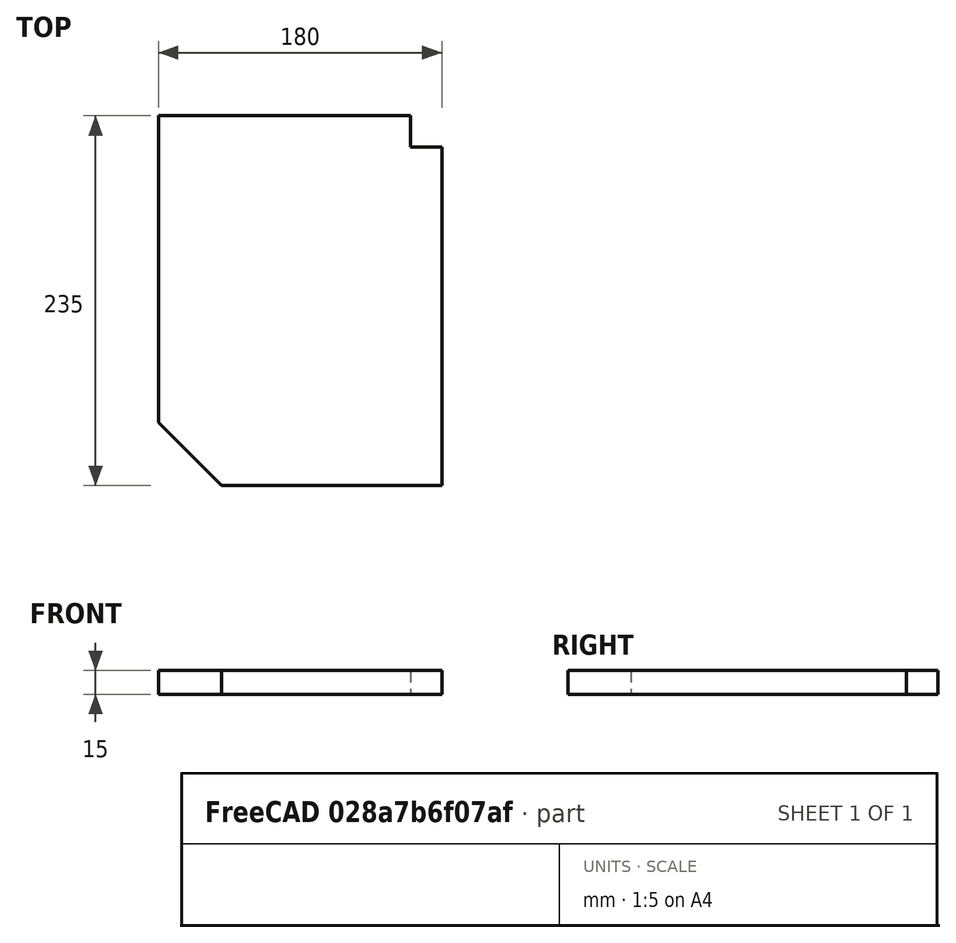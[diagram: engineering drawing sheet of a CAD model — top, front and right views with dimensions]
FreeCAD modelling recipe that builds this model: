
FCSTD DOCUMENT  (FreeCAD 0.18R4 (GitTag))
Label: RightSide-A
License: All rights reserved
LicenseURL: http://en.wikipedia.org/wiki/All_rights_reserved
objects: Sketcher::SketchObject×1, PartDesign::Pad×1, PartDesign::Body×1, App::Part×1
note: 4 computed .brp shape members not serialized (recipe doc carries the construction recipe); baked Part::Feature solids carry a one-line shape summary decoded from their .brp

FEATURE [Sketcher::SketchObject] CopySketch  label="Sketch"
  MapMode = 5
  Placement = pos=(0,0,0) rot=(1,0,0;3.14159rad)
  sketch-geometry (7):
    g0: LineSegment StartX=-180 StartY=0 StartZ=0 EndX=-180 EndY=195 EndZ=0
    g1: LineSegment StartX=-180 StartY=195 StartZ=0 EndX=-140 EndY=235 EndZ=0
    g2: LineSegment StartX=-140 StartY=235 StartZ=0 EndX=0 EndY=235 EndZ=0
    g3: LineSegment StartX=-20 StartY=0 StartZ=0 EndX=-20 EndY=20 EndZ=0
    g4: LineSegment StartX=-20 StartY=20 StartZ=0 EndX=0 EndY=20 EndZ=0
    g5: LineSegment StartX=0 StartY=235 StartZ=0 EndX=0 EndY=20 EndZ=0
    g6: LineSegment StartX=-20 StartY=0 StartZ=0 EndX=-180 EndY=0 EndZ=0
  constraints (21):
    c: Coincident(g0,g1)
    c: Coincident(g1,g2)
    c: Vertical(g0)
    c: Horizontal(g2)
    c: Distance(g0) = 195
    c: Distance(g2) = 140
    c: Coincident(g3,g4)
    c: Vertical(g3)
    c: Horizontal(g4)
    c: Distance(g4) = 20
    c: Distance(g3) = 20
    c: Distance(g5) = 215
    c: Vertical(g5)
    c: Coincident(g2,g5)
    c: Horizontal(g6)
    c: Coincident(g0,g6)
    c: Coincident(g5,g4)
    c: Distance(g6) = 160
    c: Distance(g-1,g3) = 20
    c: Distance(g-1,g4) = 20
    c: Coincident(g6,g3)
FEATURE [PartDesign::Pad] Pad
  Length = 15
  Length2 = 100
  Placement = pos=(0,0,0) rot=(1,0,0;3.14159rad)
  Profile = -> CopySketch
  Type = 0
FEATURE [PartDesign::Body] Body  label="Side"
  Group = -> [CopySketch,Pad]
  Origin = -> Origin001
  Tip = -> Pad
FEATURE [App::Part] Part
  Group = -> [Body]
  Origin = -> Origin
